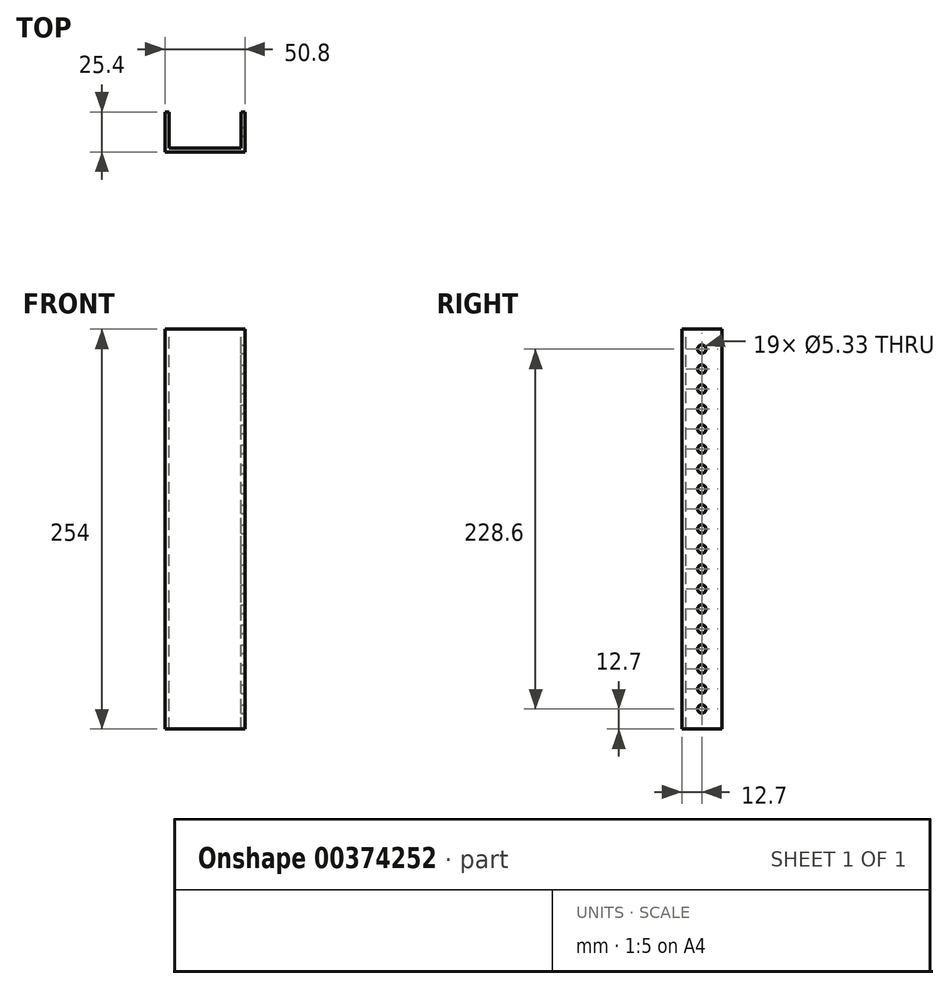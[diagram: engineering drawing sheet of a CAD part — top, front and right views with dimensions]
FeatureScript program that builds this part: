
annotation { "Feature Type Name" : "Feature", "Feature Type Description" : "" }
export const myFeature = defineFeature(function(context is Context, id is Id, definition is map)
    precondition{}
    {
        {
            var Q0;
            Q0=qCreatedBy(makeId("Front.planeOp"),FACE);
            var sketch = newSketch(context, id + "F0", { "sketchPlane" : qUnion([Q0])});
            skLineSegment(sketch, "E0.bottom", {"start": v(25.4, 127) * mm, "end": v(-25.4, 127) * mm});
            skLineSegment(sketch, "E0.top", {"start": v(25.4, -127) * mm, "end": v(-25.4, -127) * mm});
            skLineSegment(sketch, "E0.left", {"start": v(25.4, 127) * mm, "end": v(25.4, -127) * mm});
            skLineSegment(sketch, "E0.right", {"start": v(-25.4, 127) * mm, "end": v(-25.4, -127) * mm});
            skPoint(sketch, "E0.middle", {"position": v(0, 0) * mm});
            skSolve(sketch);
        }
        {
            var Q0;
            Q0=makeQuery(id+"F0.imprint","IMPRINT",FACE,{"disambiguationData":[TD([[makeQuery(id+"F0.imprint","IMPRINT",EDGE,{"derivedFrom":sQuery(id+"F0.wireOp",EDGE,"E0.bottom")}),1.0]])]});
            extrude(context, id + "F1", {"entities" : qUnion([Q0]), "endBound" : BoundingType.SYMMETRIC, "depth" : 25.4 * mm});
        }
        {
            var Q0;
            Q0=makeQuery(id+"F1.opExtrude","SWEPT_FACE",FACE,{"disambiguationData":[OSD([sQuery(id+"F0.wireOp",EDGE,"E0.bottom")])]});
            var sketch = newSketch(context, id + "F2", { "sketchPlane" : qUnion([Q0])});
            skLineSegment(sketch, "E1.bottom", {"start": v(22.86, -10.16) * mm, "end": v(-22.86, -10.16) * mm});
            skLineSegment(sketch, "E1.top", {"start": v(22.86, 12.7) * mm, "end": v(-22.86, 12.7) * mm});
            skLineSegment(sketch, "E1.left", {"start": v(22.86, -10.16) * mm, "end": v(22.86, 12.7) * mm});
            skLineSegment(sketch, "E1.right", {"start": v(-22.86, -10.16) * mm, "end": v(-22.86, 12.7) * mm});
            skPoint(sketch, "E1.middle", {"position": v(0, 0) * mm});
            skSolve(sketch);
        }
        {
            var Q0;
            Q0=makeQuery(id+"F2.imprint","IMPRINT",FACE,{"disambiguationData":[TD([[makeQuery(id+"F2.imprint","IMPRINT",EDGE,{"derivedFrom":sQuery(id+"F2.wireOp",EDGE,"E1.bottom")}),-1.0]])]});
            extrude(context, id + "F3", {"entities" : qUnion([Q0]), "operationType" : NewBodyOperationType.REMOVE, "endBound" : BoundingType.THROUGH_ALL, "oppositeDirection" : true, "depth" : 25.4 * mm});
        }
        {
            var Q0;
            Q0=makeQuery(id+"F1.opExtrude","SWEPT_FACE",FACE,{"disambiguationData":[OSD([sQuery(id+"F0.wireOp",EDGE,"E0.left")])]});
            var sketch = newSketch(context, id + "F4", { "sketchPlane" : qUnion([Q0])});
            skCircle(sketch, "E2", {"center": v(0, 114.3) * mm, "radius": 2.67 * mm});
            skPoint(sketch, "E2.centerSnap0", {"position": v(0, 127) * mm});
            skCircle(sketch, "E3.1.0.0", {"center": v(0, 101.6) * mm, "radius": 2.67 * mm});
            skCircle(sketch, "E3.2.0.0", {"center": v(0, 88.9) * mm, "radius": 2.67 * mm});
            skCircle(sketch, "E3.3.0.0", {"center": v(0, 76.2) * mm, "radius": 2.67 * mm});
            skCircle(sketch, "E3.4.0.0", {"center": v(0, 63.5) * mm, "radius": 2.67 * mm});
            skCircle(sketch, "E3.5.0.0", {"center": v(0, 50.8) * mm, "radius": 2.67 * mm});
            skCircle(sketch, "E3.6.0.0", {"center": v(0, 38.1) * mm, "radius": 2.67 * mm});
            skCircle(sketch, "E3.7.0.0", {"center": v(0, 25.4) * mm, "radius": 2.67 * mm});
            skCircle(sketch, "E3.8.0.0", {"center": v(0, 12.7) * mm, "radius": 2.67 * mm});
            skCircle(sketch, "E3.9.0.0", {"center": v(0, 0) * mm, "radius": 2.67 * mm});
            skCircle(sketch, "E3.10.0.0", {"center": v(0, -12.7) * mm, "radius": 2.67 * mm});
            skCircle(sketch, "E3.11.0.0", {"center": v(0, -25.4) * mm, "radius": 2.67 * mm});
            skCircle(sketch, "E3.12.0.0", {"center": v(0, -38.1) * mm, "radius": 2.67 * mm});
            skCircle(sketch, "E3.13.0.0", {"center": v(0, -50.8) * mm, "radius": 2.67 * mm});
            skCircle(sketch, "E3.14.0.0", {"center": v(0, -63.5) * mm, "radius": 2.67 * mm});
            skCircle(sketch, "E3.15.0.0", {"center": v(0, -76.2) * mm, "radius": 2.67 * mm});
            skCircle(sketch, "E3.16.0.0", {"center": v(0, -88.9) * mm, "radius": 2.67 * mm});
            skCircle(sketch, "E3.17.0.0", {"center": v(0, -101.6) * mm, "radius": 2.67 * mm});
            skCircle(sketch, "E3.18.0.0", {"center": v(0, -114.3) * mm, "radius": 2.67 * mm});
            skLineSegment(sketch, "E3.direction1", {"start": v(0, 114.3) * mm, "end": v(0, 101.6) * mm, "construction": true});
            skSolve(sketch);
        }
        {
            var Q0;
            Q0=makeQuery(id+"F4.imprint","IMPRINT",FACE,{"disambiguationData":[TD([[makeQuery(id+"F4.imprint","IMPRINT",EDGE,{"derivedFrom":sQuery(id+"F4.wireOp",EDGE,"E3.1.0.0")}),1.0]])]});
            var Q1;
            Q1=makeQuery(id+"F4.imprint","IMPRINT",FACE,{"disambiguationData":[TD([[makeQuery(id+"F4.imprint","IMPRINT",EDGE,{"derivedFrom":sQuery(id+"F4.wireOp",EDGE,"E3.6.0.0")}),1.0]])]});
            var Q2;
            Q2=makeQuery(id+"F4.imprint","IMPRINT",FACE,{"disambiguationData":[TD([[makeQuery(id+"F4.imprint","IMPRINT",EDGE,{"derivedFrom":sQuery(id+"F4.wireOp",EDGE,"E3.5.0.0")}),1.0]])]});
            var Q3;
            Q3=makeQuery(id+"F4.imprint","IMPRINT",FACE,{"disambiguationData":[TD([[makeQuery(id+"F4.imprint","IMPRINT",EDGE,{"derivedFrom":sQuery(id+"F4.wireOp",EDGE,"E3.4.0.0")}),1.0]])]});
            var Q4;
            Q4=makeQuery(id+"F4.imprint","IMPRINT",FACE,{"disambiguationData":[TD([[makeQuery(id+"F4.imprint","IMPRINT",EDGE,{"derivedFrom":sQuery(id+"F4.wireOp",EDGE,"E3.3.0.0")}),1.0]])]});
            var Q5;
            Q5=makeQuery(id+"F4.imprint","IMPRINT",FACE,{"disambiguationData":[TD([[makeQuery(id+"F4.imprint","IMPRINT",EDGE,{"derivedFrom":sQuery(id+"F4.wireOp",EDGE,"E2")}),1.0]])]});
            var Q6;
            Q6=makeQuery(id+"F4.imprint","IMPRINT",FACE,{"disambiguationData":[TD([[makeQuery(id+"F4.imprint","IMPRINT",EDGE,{"derivedFrom":sQuery(id+"F4.wireOp",EDGE,"E3.14.0.0")}),1.0]])]});
            var Q7;
            Q7=makeQuery(id+"F4.imprint","IMPRINT",FACE,{"disambiguationData":[TD([[makeQuery(id+"F4.imprint","IMPRINT",EDGE,{"derivedFrom":sQuery(id+"F4.wireOp",EDGE,"E3.16.0.0")}),1.0]])]});
            var Q8;
            Q8=makeQuery(id+"F4.imprint","IMPRINT",FACE,{"disambiguationData":[TD([[makeQuery(id+"F4.imprint","IMPRINT",EDGE,{"derivedFrom":sQuery(id+"F4.wireOp",EDGE,"E3.15.0.0")}),1.0]])]});
            var Q9;
            Q9=makeQuery(id+"F4.imprint","IMPRINT",FACE,{"disambiguationData":[TD([[makeQuery(id+"F4.imprint","IMPRINT",EDGE,{"derivedFrom":sQuery(id+"F4.wireOp",EDGE,"E3.18.0.0")}),1.0]])]});
            var Q10;
            Q10=makeQuery(id+"F4.imprint","IMPRINT",FACE,{"disambiguationData":[TD([[makeQuery(id+"F4.imprint","IMPRINT",EDGE,{"derivedFrom":sQuery(id+"F4.wireOp",EDGE,"E3.17.0.0")}),1.0]])]});
            var Q11;
            Q11=makeQuery(id+"F4.imprint","IMPRINT",FACE,{"disambiguationData":[TD([[makeQuery(id+"F4.imprint","IMPRINT",EDGE,{"derivedFrom":sQuery(id+"F4.wireOp",EDGE,"E3.2.0.0")}),1.0]])]});
            var Q12;
            Q12=makeQuery(id+"F4.imprint","IMPRINT",FACE,{"disambiguationData":[TD([[makeQuery(id+"F4.imprint","IMPRINT",EDGE,{"derivedFrom":sQuery(id+"F4.wireOp",EDGE,"E3.13.0.0")}),1.0]])]});
            var Q13;
            Q13=makeQuery(id+"F4.imprint","IMPRINT",FACE,{"disambiguationData":[TD([[makeQuery(id+"F4.imprint","IMPRINT",EDGE,{"derivedFrom":sQuery(id+"F4.wireOp",EDGE,"E3.7.0.0")}),1.0]])]});
            var Q14;
            Q14=makeQuery(id+"F4.imprint","IMPRINT",FACE,{"disambiguationData":[TD([[makeQuery(id+"F4.imprint","IMPRINT",EDGE,{"derivedFrom":sQuery(id+"F4.wireOp",EDGE,"E3.8.0.0")}),1.0]])]});
            var Q15;
            Q15=makeQuery(id+"F4.imprint","IMPRINT",FACE,{"disambiguationData":[TD([[makeQuery(id+"F4.imprint","IMPRINT",EDGE,{"derivedFrom":sQuery(id+"F4.wireOp",EDGE,"E3.10.0.0")}),1.0]])]});
            var Q16;
            Q16=makeQuery(id+"F4.imprint","IMPRINT",FACE,{"disambiguationData":[TD([[makeQuery(id+"F4.imprint","IMPRINT",EDGE,{"derivedFrom":sQuery(id+"F4.wireOp",EDGE,"E3.11.0.0")}),1.0]])]});
            var Q17;
            Q17=makeQuery(id+"F4.imprint","IMPRINT",FACE,{"disambiguationData":[TD([[makeQuery(id+"F4.imprint","IMPRINT",EDGE,{"derivedFrom":sQuery(id+"F4.wireOp",EDGE,"E3.12.0.0")}),1.0]])]});
            var Q18;
            Q18=makeQuery(id+"F4.imprint","IMPRINT",FACE,{"disambiguationData":[TD([[makeQuery(id+"F4.imprint","IMPRINT",EDGE,{"derivedFrom":sQuery(id+"F4.wireOp",EDGE,"E3.9.0.0")}),1.0]])]});
            var Q19;
            Q19=sQuery(id+"F4.wireOp",EDGE,"E3.12.0.0");
            var Q20;
            Q20=sQuery(id+"F4.wireOp",EDGE,"E3.11.0.0");
            var Q21;
            Q21=sQuery(id+"F4.wireOp",EDGE,"E3.9.0.0");
            var Q22;
            Q22=sQuery(id+"F4.wireOp",EDGE,"E3.7.0.0");
            var Q23;
            Q23=sQuery(id+"F4.wireOp",EDGE,"E3.6.0.0");
            var Q24;
            Q24=sQuery(id+"F4.wireOp",EDGE,"E3.5.0.0");
            var Q25;
            Q25=sQuery(id+"F4.wireOp",EDGE,"E3.4.0.0");
            var Q26;
            Q26=sQuery(id+"F4.wireOp",EDGE,"E3.2.0.0");
            var Q27;
            Q27=sQuery(id+"F4.wireOp",EDGE,"E3.1.0.0");
            var Q28;
            Q28=sQuery(id+"F4.wireOp",EDGE,"E3.15.0.0");
            var Q29;
            Q29=sQuery(id+"F4.wireOp",EDGE,"E2");
            var Q30;
            Q30=sQuery(id+"F4.wireOp",EDGE,"E3.13.0.0");
            var Q31;
            Q31=sQuery(id+"F4.wireOp",EDGE,"E3.8.0.0");
            var Q32;
            Q32=sQuery(id+"F4.wireOp",EDGE,"E3.10.0.0");
            var Q33;
            Q33=sQuery(id+"F4.wireOp",EDGE,"E3.17.0.0");
            var Q34;
            Q34=sQuery(id+"F4.wireOp",EDGE,"E3.16.0.0");
            var Q35;
            Q35=sQuery(id+"F4.wireOp",EDGE,"E3.14.0.0");
            var Q36;
            Q36=sQuery(id+"F4.wireOp",EDGE,"E3.3.0.0");
            var Q37;
            Q37=sQuery(id+"F4.wireOp",EDGE,"E3.18.0.0");
            extrude(context, id + "F5", {"entities" : qUnion([Q0, Q1, Q2, Q3, Q4, Q5, Q6, Q7, Q8, Q9, Q10, Q11, Q12, Q13, Q14, Q15, Q16, Q17, Q18]), "operationType" : NewBodyOperationType.REMOVE, "surfaceEntities" : qUnion([Q19, Q20, Q21, Q22, Q23, Q24, Q25, Q26, Q27, Q28, Q29, Q30, Q31, Q32, Q33, Q34, Q35, Q36, Q37]), "oppositeDirection" : true, "depth" : 2.54 * mm});
        }
    });
